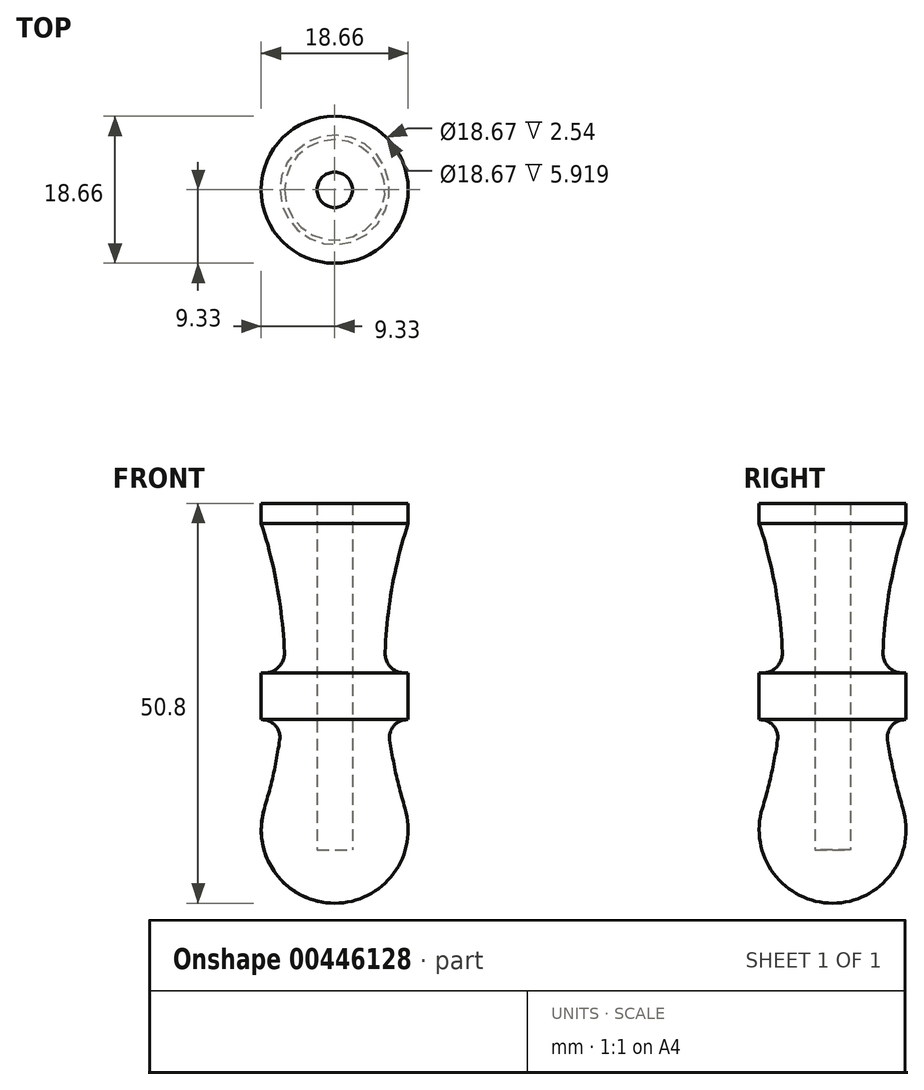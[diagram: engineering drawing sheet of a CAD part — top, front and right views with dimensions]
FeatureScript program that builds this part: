
annotation { "Feature Type Name" : "Feature", "Feature Type Description" : "" }
export const myFeature = defineFeature(function(context is Context, id is Id, definition is map)
    precondition{}
    {
        {
            var Q0;
            Q0=qCreatedBy(makeId("Front.planeOp"),FACE);
            var sketch = newSketch(context, id + "F0", { "sketchPlane" : qUnion([Q0])});
            skArc(sketch, "E0", {"start": v(-8.93, 12.04) * mm, "mid": v(-7.5, 3.77) * mm, "end": v(0, 0) * mm});
            skLineSegment(sketch, "E1.right", {"start": v(-9.33, 48.26) * mm, "end": v(-9.33, 50.8) * mm});
            skPoint(sketch, "E1.middle", {"position": v(0, 49.53) * mm});
            skLineSegment(sketch, "E2", {"start": v(0, 49.53) * mm, "end": v(0, 9.33) * mm, "construction": true});
            skArc(sketch, "E3", {"start": v(-8.93, 12.04) * mm, "mid": v(-7.8, 16.37) * mm, "end": v(-6.98, 20.77) * mm});
            skLineSegment(sketch, "E4.right", {"start": v(-2.25, 6.74) * mm, "end": v(-2.25, 50.8) * mm});
            skLineSegment(sketch, "E5.trimOffspring", {"start": v(-2.25, 50.8) * mm, "end": v(-9.33, 50.8) * mm});
            skLineSegment(sketch, "E6.bottom", {"start": v(-9.18, 23.32) * mm, "end": v(-9.33, 23.32) * mm});
            skLineSegment(sketch, "E6.right", {"start": v(-9.33, 23.32) * mm, "end": v(-9.33, 29.23) * mm});
            skPoint(sketch, "E6.middle", {"position": v(0, 25.4) * mm});
            skArc(sketch, "E7.trimOffspring", {"start": v(-6.4, 31.87) * mm, "mid": v(-7.3, 40.17) * mm, "end": v(-9.33, 48.26) * mm});
            skArc(sketch, "E8.filletArc", {"start": v(-6.98, 20.77) * mm, "mid": v(-7.5, 22.55) * mm, "end": v(-9.18, 23.32) * mm});
            skPoint(sketch, "E9.newPointA", {"position": v(-8.43, 28.58) * mm});
            skLineSegment(sketch, "E10", {"start": v(-9.33, 29.23) * mm, "end": v(-8.93, 29.23) * mm});
            skPoint(sketch, "E11.visualSharp", {"position": v(-6.35, 29.23) * mm});
            skArc(sketch, "E11.filletArc", {"start": v(-8.93, 29.23) * mm, "mid": v(-7.1, 30.01) * mm, "end": v(-6.4, 31.87) * mm});
            skLineSegment(sketch, "E12", {"start": v(0, 6.74) * mm, "end": v(-2.25, 6.74) * mm});
            skLineSegment(sketch, "E13", {"start": v(0, 6.74) * mm, "end": v(0, 0) * mm});
            skSolve(sketch);
        }
        {
            var Q0;
            Q0=sQuery(id+"F0.wireOp",EDGE,"E4.right");
            var Q1;
            Q1=sQuery(id+"F0.wireOp",EDGE,"E5.trimOffspring");
            var Q2;
            Q2=sQuery(id+"F0.wireOp",EDGE,"E1.right");
            var Q3;
            Q3=sQuery(id+"F0.wireOp",EDGE,"E7.trimOffspring");
            var Q4;
            Q4=sQuery(id+"F0.wireOp",EDGE,"E11.filletArc");
            var Q5;
            Q5=sQuery(id+"F0.wireOp",EDGE,"E10");
            var Q6;
            Q6=sQuery(id+"F0.wireOp",EDGE,"E6.right");
            var Q7;
            Q7=sQuery(id+"F0.wireOp",EDGE,"E6.bottom");
            var Q8;
            Q8=sQuery(id+"F0.wireOp",EDGE,"E8.filletArc");
            var Q9;
            Q9=sQuery(id+"F0.wireOp",EDGE,"E3");
            var Q10;
            Q10=sQuery(id+"F0.wireOp",EDGE,"E0");
            var Q11;
            Q11=sQuery(id+"F0.wireOp",EDGE,"E12");
            var Q12;
            Q12=sQuery(id+"F0.wireOp",EDGE,"E2");
            revolve(context, id + "F1", {"bodyType" : ToolBodyType.SURFACE, "surfaceEntities" : qUnion([Q0, Q1, Q2, Q3, Q4, Q5, Q6, Q7, Q8, Q9, Q10, Q11]), "axis" : qUnion([Q12]), "revolveType" : RevolveType.FULL});
        }
    });
